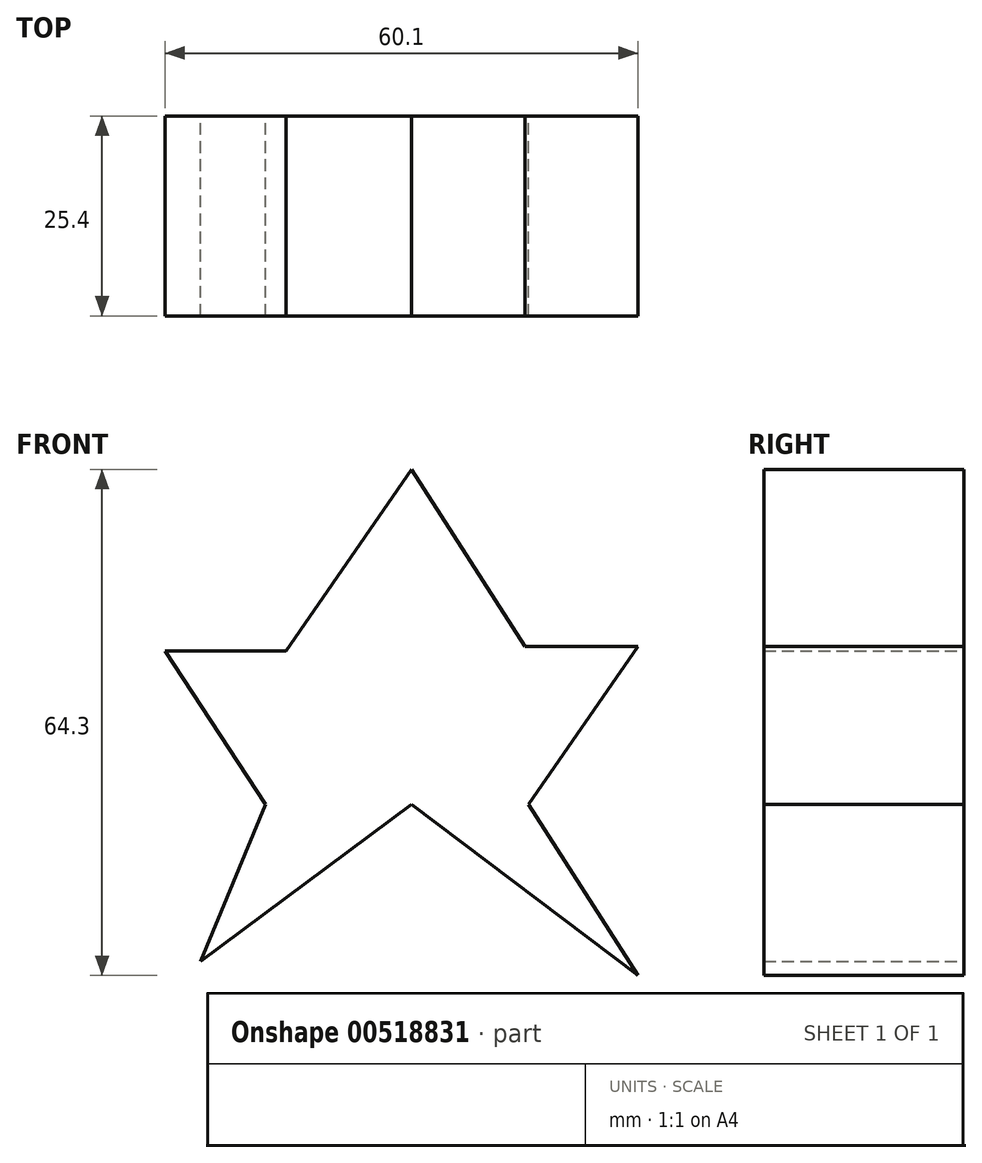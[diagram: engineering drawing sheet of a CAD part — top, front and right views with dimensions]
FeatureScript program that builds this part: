
annotation { "Feature Type Name" : "Feature", "Feature Type Description" : "" }
export const myFeature = defineFeature(function(context is Context, id is Id, definition is map)
    precondition{}
    {
        {
            var Q0;
            Q0=qCreatedBy(makeId("Front.planeOp"),FACE);
            var sketch = newSketch(context, id + "F0", { "sketchPlane" : qUnion([Q0])});
            skLineSegment(sketch, "E0", {"start": v(0, 42.57) * mm, "end": v(-15.96, 19.5) * mm});
            skLineSegment(sketch, "E1", {"start": v(0, 42.57) * mm, "end": v(14.39, 20.1) * mm});
            skLineSegment(sketch, "E2", {"start": v(-15.96, 19.5) * mm, "end": v(-31.33, 19.5) * mm});
            skLineSegment(sketch, "E3", {"start": v(14.39, 20.1) * mm, "end": v(28.77, 20.1) * mm});
            skLineSegment(sketch, "E4", {"start": v(28.77, 20.1) * mm, "end": v(14.86, 0) * mm});
            skLineSegment(sketch, "E5", {"start": v(14.86, 0) * mm, "end": v(28.77, -21.73) * mm});
            skLineSegment(sketch, "E6", {"start": v(28.77, -21.73) * mm, "end": v(0, 0) * mm});
            skLineSegment(sketch, "E7", {"start": v(0, 0) * mm, "end": v(-26.8, -19.9) * mm});
            skLineSegment(sketch, "E8", {"start": v(-26.8, -19.9) * mm, "end": v(-18.52, 0) * mm});
            skLineSegment(sketch, "E9", {"start": v(-18.52, 0) * mm, "end": v(-31.33, 19.5) * mm});
            skSolve(sketch);
        }
        {
            var Q0;
            Q0 = qSketchRegion(id + "F0", true);
            extrude(context, id + "F1", {"entities" : qUnion([Q0]), "depth" : 25.4 * mm});
        }
    });
